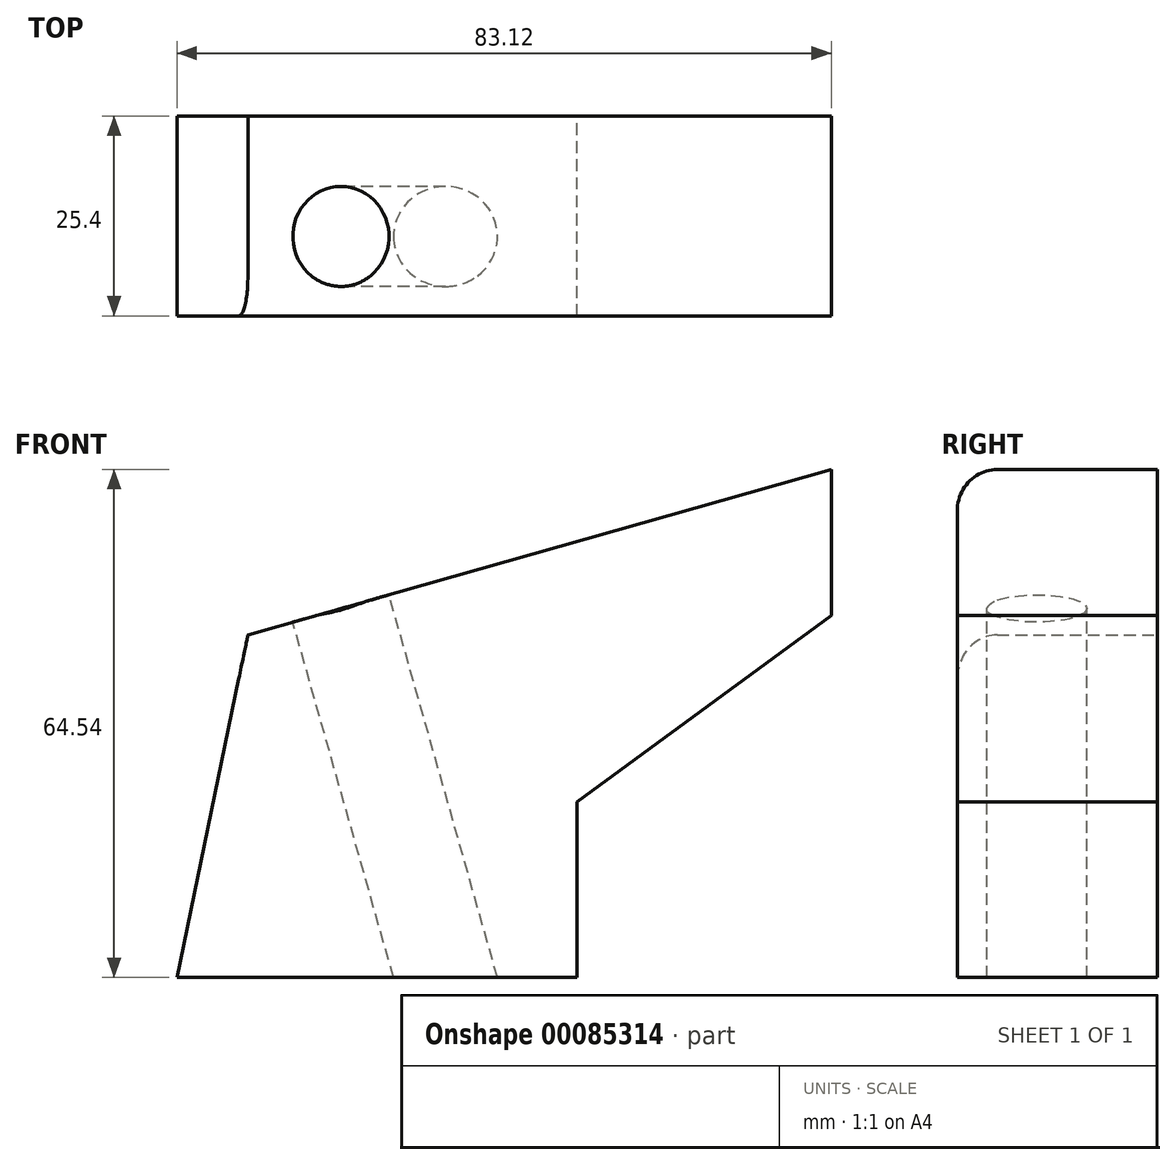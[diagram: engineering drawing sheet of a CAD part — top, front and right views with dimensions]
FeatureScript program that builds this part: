
annotation { "Feature Type Name" : "Feature", "Feature Type Description" : "" }
export const myFeature = defineFeature(function(context is Context, id is Id, definition is map)
    precondition{}
    {
        {
            var Q0;
            Q0=qCreatedBy(makeId("Front.planeOp"),FACE);
            var sketch = newSketch(context, id + "F0", { "sketchPlane" : qUnion([Q0])});
            skLineSegment(sketch, "E0", {"start": v(-12.78, 10.8) * mm, "end": v(19.54, 34.45) * mm});
            skLineSegment(sketch, "E1", {"start": v(19.54, 34.45) * mm, "end": v(19.54, 53.02) * mm});
            skLineSegment(sketch, "E2", {"start": v(19.54, 53.02) * mm, "end": v(-54.57, 32) * mm});
            skLineSegment(sketch, "E3", {"start": v(-54.57, 32) * mm, "end": v(-63.58, -11.52) * mm});
            skLineSegment(sketch, "E4", {"start": v(-63.58, -11.52) * mm, "end": v(-12.78, -11.52) * mm});
            skLineSegment(sketch, "E5", {"start": v(-12.78, -11.52) * mm, "end": v(-12.78, 10.8) * mm});
            skSolve(sketch);
        }
        {
            var Q0;
            Q0=makeQuery(id+"F0.imprint","IMPRINT",FACE,{"disambiguationData":[TD([[makeQuery(id+"F0.imprint","IMPRINT",EDGE,{"derivedFrom":sQuery(id+"F0.wireOp",EDGE,"E0")}),1.0]])]});
            extrude(context, id + "F1", {"entities" : qUnion([Q0]), "depth" : 25.4 * mm});
        }
        {
            var Q0;
            Q0=makeQuery(id+"F1.opExtrude","SWEPT_FACE",FACE,{"disambiguationData":[OSD([sQuery(id+"F0.wireOp",EDGE,"E2")])]});
            var sketch = newSketch(context, id + "F2", { "sketchPlane" : qUnion([Q0])});
            skCircle(sketch, "E6", {"center": v(-31.5, -15.3) * mm, "radius": 6.35 * mm});
            skSolve(sketch);
        }
        {
            var Q0;
            Q0=makeQuery(id+"F2.imprint","IMPRINT",FACE,{"disambiguationData":[TD([[makeQuery(id+"F2.imprint","IMPRINT",EDGE,{"derivedFrom":sQuery(id+"F2.wireOp",EDGE,"E6")}),1.0]])]});
            extrude(context, id + "F3", {"entities" : qUnion([Q0]), "operationType" : NewBodyOperationType.REMOVE, "endBound" : BoundingType.THROUGH_ALL, "oppositeDirection" : true, "depth" : 25.4 * mm});
        }
        {
            var Q0;
            Q0=makeQuery(id+"F1.opExtrude","CAP_EDGE",EDGE,{"disambiguationData":[OSD([sQuery(id+"F0.wireOp",EDGE,"E2")])],"isStart":false});
            fillet(context, id + "F4", {"entities" : qUnion([Q0]), "radius" : 5.08 * mm, "tangentPropagation" : true, "allowEdgeOverflow" : false});
        }
    });
